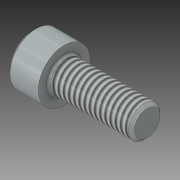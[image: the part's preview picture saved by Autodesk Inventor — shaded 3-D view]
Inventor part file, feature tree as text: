
AUTODESK INVENTOR PART (.ipt)
format: ipt  version: 2016 SP1 (Build 200210100, 210)  size: 131,584 bytes
history: native  units: in
note: dims shown in document units (in); Inventor stores cm internally (conversion verified against a paired STEP export)
features: thread x1, other x1
ambient origin geometry x8: Origin, YZ Plane, XZ Plane, XY Plane, X Axis, Y Axis, Z Axis, Center Point
bodies: Solid1 (feature_tree)
feature tree (2):
  thread  "Thread1"  [1 undecoded]
  other  "Hex"
note: 1 required parameter value undecoded (feature->parameter linkage not recoverable at this tier; creation-order binding heuristic only, values carry confidence <= 0.55)
